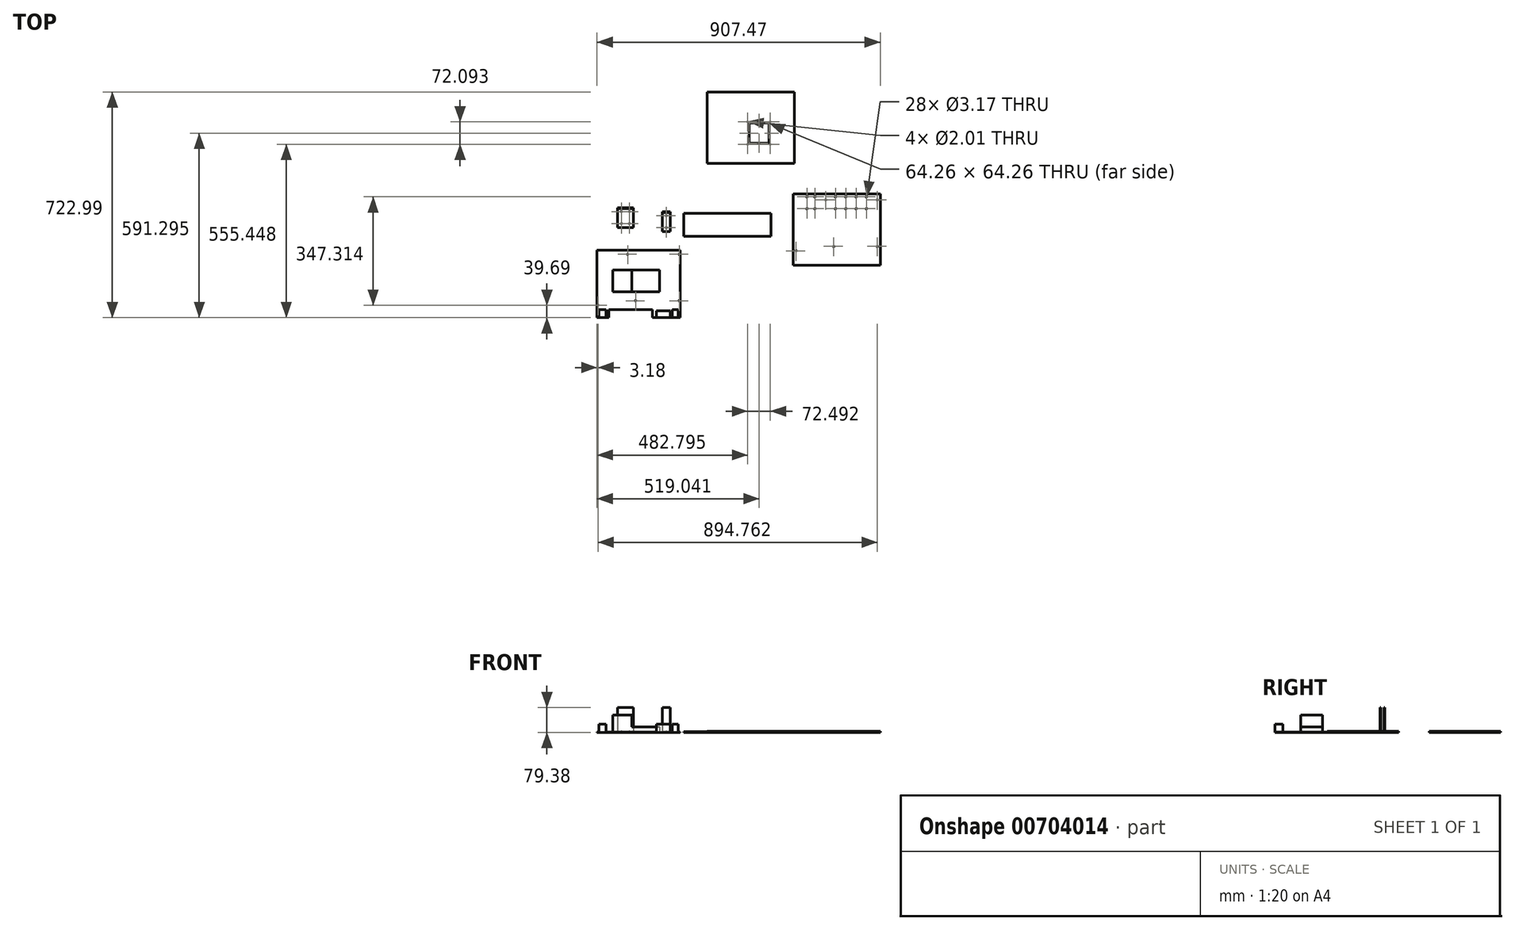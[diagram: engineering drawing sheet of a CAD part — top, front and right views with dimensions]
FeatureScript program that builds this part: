
annotation { "Feature Type Name" : "Feature", "Feature Type Description" : "" }
export const myFeature = defineFeature(function(context is Context, id is Id, definition is map)
    precondition{}
    {
        {
            var Q0;
            Q0=qCreatedBy(makeId("Top.planeOp"),FACE);
            var sketch = newSketch(context, id + "F0", { "sketchPlane" : qUnion([Q0])});
            skLineSegment(sketch, "E0.bottom", {"start": v(-132.8, 35.4) * mm, "end": v(133.9, 35.4) * mm});
            skLineSegment(sketch, "E0.left", {"start": v(-132.8, 35.4) * mm, "end": v(-132.8, -180.5) * mm});
            skLineSegment(sketch, "E0.right", {"start": v(133.9, 35.4) * mm, "end": v(133.9, -180.5) * mm});
            skPoint(sketch, "E1", {"position": v(-94.7, -180.5) * mm});
            skPoint(sketch, "E2", {"position": v(-94.7, -155.1) * mm});
            skLineSegment(sketch, "E3", {"start": v(-94.7, -155.1) * mm, "end": v(-94.7, -180.5) * mm});
            skPoint(sketch, "E4", {"position": v(45, -155.1) * mm});
            skPoint(sketch, "E5", {"position": v(45, -180.5) * mm});
            skLineSegment(sketch, "E6", {"start": v(-94.7, -155.1) * mm, "end": v(45, -155.1) * mm});
            skLineSegment(sketch, "E7", {"start": v(-94.7, -180.5) * mm, "end": v(-132.8, -180.5) * mm});
            skLineSegment(sketch, "E8", {"start": v(45, -180.5) * mm, "end": v(133.9, -180.5) * mm});
            skLineSegment(sketch, "E9", {"start": v(45, -155.1) * mm, "end": v(45, -180.5) * mm});
            skSolve(sketch);
        }
        {
            var Q0;
            Q0=makeQuery(id+"F0.imprint","IMPRINT",FACE,{"disambiguationData":[TD([[makeQuery(id+"F0.imprint","IMPRINT",EDGE,{"derivedFrom":sQuery(id+"F0.wireOp",EDGE,"E0.bottom")}),-1.0]])]});
            var Q1;
            Q1 = qSketchRegion(id + "F15", true);
            extrude(context, id + "F1", {"entities" : qUnion([Q0, Q1]), "depth" : 1.59 * mm, "offsetDistance" : 25.4 * mm});
        }
        {
            var Q0;
            Q0=makeQuery(id+"F1.opExtrude","CAP_FACE",FACE,{"disambiguationData":[OSD([sQuery(id+"F0.wireOp",EDGE,"E0.bottom"),sQuery(id+"F0.wireOp",EDGE,"E0.left"),sQuery(id+"F0.wireOp",EDGE,"E0.right"),sQuery(id+"F0.wireOp",EDGE,"E3"),sQuery(id+"F0.wireOp",EDGE,"E6"),sQuery(id+"F0.wireOp",EDGE,"E7"),sQuery(id+"F0.wireOp",EDGE,"E8"),sQuery(id+"F0.wireOp",EDGE,"E9")])],"isStart":false});
            var sketch = newSketch(context, id + "F2", { "sketchPlane" : qUnion([Q0])});
            skPoint(sketch, "E10", {"position": v(-132.8, -180.5) * mm});
            skPoint(sketch, "E11", {"position": v(-126.45, -180.5) * mm});
            skPoint(sketch, "E12", {"position": v(-126.45, -155.1) * mm});
            skPoint(sketch, "E13", {"position": v(-104.22, -155.1) * mm});
            skPoint(sketch, "E14", {"position": v(-104.22, -180.5) * mm});
            skLineSegment(sketch, "E15", {"start": v(-126.45, -155.1) * mm, "end": v(-104.22, -155.1) * mm});
            skLineSegment(sketch, "E16", {"start": v(-104.22, -155.1) * mm, "end": v(-104.22, -180.5) * mm});
            skLineSegment(sketch, "E17", {"start": v(-104.22, -180.5) * mm, "end": v(-126.45, -180.5) * mm});
            skLineSegment(sketch, "E18", {"start": v(-126.45, -180.5) * mm, "end": v(-126.45, -155.1) * mm});
            skLineSegment(sketch, "E19", {"start": v(-132.8, -180.5) * mm, "end": v(-126.45, -180.5) * mm});
            skPoint(sketch, "E20", {"position": v(-94.7, -180.5) * mm});
            skLineSegment(sketch, "E21", {"start": v(-94.7, -180.5) * mm, "end": v(-104.22, -180.5) * mm});
            skPoint(sketch, "E22", {"position": v(57.7, -180.5) * mm});
            skPoint(sketch, "E23", {"position": v(45, -180.5) * mm});
            skPoint(sketch, "E24", {"position": v(102.15, -180.5) * mm});
            skPoint(sketch, "E25", {"position": v(108.5, -180.5) * mm});
            skPoint(sketch, "E26", {"position": v(127.55, -180.5) * mm});
            skPoint(sketch, "E27", {"position": v(133.9, -180.5) * mm});
            skPoint(sketch, "E28", {"position": v(57.7, -158.28) * mm});
            skPoint(sketch, "E29", {"position": v(102.15, -158.28) * mm});
            skPoint(sketch, "E30", {"position": v(108.4, -155.1) * mm});
            skPoint(sketch, "E31", {"position": v(127.55, -155.1) * mm});
            skLineSegment(sketch, "E32", {"start": v(57.7, -180.5) * mm, "end": v(57.7, -158.28) * mm});
            skLineSegment(sketch, "E33", {"start": v(102.15, -158.28) * mm, "end": v(57.7, -158.28) * mm});
            skLineSegment(sketch, "E34", {"start": v(102.15, -180.5) * mm, "end": v(102.15, -158.28) * mm});
            skLineSegment(sketch, "E35", {"start": v(108.4, -155.1) * mm, "end": v(108.5, -180.5) * mm});
            skLineSegment(sketch, "E36", {"start": v(108.4, -155.1) * mm, "end": v(127.55, -155.1) * mm});
            skLineSegment(sketch, "E37", {"start": v(127.55, -180.5) * mm, "end": v(127.55, -155.1) * mm});
            skLineSegment(sketch, "E38", {"start": v(108.5, -180.5) * mm, "end": v(127.55, -180.5) * mm});
            skLineSegment(sketch, "E39", {"start": v(102.15, -180.5) * mm, "end": v(57.7, -180.5) * mm});
            skSolve(sketch);
        }
        {
            var Q0;
            Q0=makeQuery(id+"F2.imprint","IMPRINT",FACE,{"disambiguationData":[TD([[makeQuery(id+"F2.imprint","IMPRINT",EDGE,{"derivedFrom":sQuery(id+"F2.wireOp",EDGE,"E15")}),-1.0]])]});
            extrude(context, id + "F3", {"entities" : qUnion([Q0]), "operationType" : NewBodyOperationType.ADD, "depth" : 22.22 * mm, "offsetDistance" : 25.4 * mm});
        }
        {
            var Q0;
            Q0 = qSketchRegion(id + "F2", true);
            extrude(context, id + "F4", {"entities" : qUnion([Q0]), "operationType" : NewBodyOperationType.ADD, "depth" : 25.4 * mm, "offsetDistance" : 25.4 * mm});
        }
        {
            var Q0;
            Q0=makeQuery(id+"F1.opExtrude","CAP_FACE",FACE,{"disambiguationData":[OSD([sQuery(id+"F0.wireOp",EDGE,"E0.bottom"),sQuery(id+"F0.wireOp",EDGE,"E0.left"),sQuery(id+"F0.wireOp",EDGE,"E0.right"),sQuery(id+"F0.wireOp",EDGE,"E3"),sQuery(id+"F0.wireOp",EDGE,"E6"),sQuery(id+"F0.wireOp",EDGE,"E7"),sQuery(id+"F0.wireOp",EDGE,"E8"),sQuery(id+"F0.wireOp",EDGE,"E9")])],"isStart":false});
            var sketch = newSketch(context, id + "F5", { "sketchPlane" : qUnion([Q0])});
            skPoint(sketch, "E40", {"position": v(-82, -97.96) * mm});
            skPoint(sketch, "E41", {"position": v(-82, -28.1) * mm});
            skPoint(sketch, "E42", {"position": v(-21.67, -28.1) * mm});
            skPoint(sketch, "E43", {"position": v(-21.67, -97.96) * mm});
            skLineSegment(sketch, "E44", {"start": v(-82, -97.96) * mm, "end": v(-21.67, -97.96) * mm});
            skLineSegment(sketch, "E45", {"start": v(-21.67, -28.1) * mm, "end": v(-21.67, -97.96) * mm});
            skLineSegment(sketch, "E46", {"start": v(-21.67, -28.1) * mm, "end": v(-82, -28.1) * mm});
            skLineSegment(sketch, "E47", {"start": v(-82, -97.96) * mm, "end": v(-82, -28.1) * mm});
            skPoint(sketch, "E48", {"position": v(67.23, -97.96) * mm});
            skPoint(sketch, "E49", {"position": v(67.23, -28.1) * mm});
            skLineSegment(sketch, "E50", {"start": v(-21.67, -97.96) * mm, "end": v(67.23, -97.96) * mm});
            skLineSegment(sketch, "E51", {"start": v(67.23, -28.1) * mm, "end": v(67.23, -97.96) * mm});
            skLineSegment(sketch, "E52", {"start": v(67.23, -28.1) * mm, "end": v(-21.67, -28.1) * mm});
            skSolve(sketch);
        }
        {
            var Q0;
            Q0=makeQuery(id+"F5.imprint","IMPRINT",FACE,{"disambiguationData":[TD([[makeQuery(id+"F5.imprint","IMPRINT",EDGE,{"derivedFrom":sQuery(id+"F5.wireOp",EDGE,"E45")}),1.0]])]});
            extrude(context, id + "F6", {"entities" : qUnion([Q0]), "operationType" : NewBodyOperationType.ADD, "depth" : 15.88 * mm, "offsetDistance" : 25.4 * mm});
        }
        {
            var Q0;
            Q0=makeQuery(id+"F1.opExtrude","CAP_FACE",FACE,{"disambiguationData":[OSD([sQuery(id+"F0.wireOp",EDGE,"E0.bottom"),sQuery(id+"F0.wireOp",EDGE,"E0.left"),sQuery(id+"F0.wireOp",EDGE,"E0.right"),sQuery(id+"F0.wireOp",EDGE,"E3"),sQuery(id+"F0.wireOp",EDGE,"E6"),sQuery(id+"F0.wireOp",EDGE,"E7"),sQuery(id+"F0.wireOp",EDGE,"E8"),sQuery(id+"F0.wireOp",EDGE,"E9")])],"isStart":false});
            var sketch = newSketch(context, id + "F7", { "sketchPlane" : qUnion([Q0])});
            skPoint(sketch, "E53", {"position": v(-82, -97.96) * mm});
            skPoint(sketch, "E54", {"position": v(-82, -28.1) * mm});
            skLineSegment(sketch, "E55", {"start": v(-82, -97.96) * mm, "end": v(-21.67, -97.96) * mm});
            skLineSegment(sketch, "E56", {"start": v(-21.67, -28.1) * mm, "end": v(-82, -28.1) * mm});
            skLineSegment(sketch, "E57", {"start": v(-82, -97.96) * mm, "end": v(-82, -28.1) * mm});
            skLineSegment(sketch, "E58", {"start": v(-21.67, -97.96) * mm, "end": v(-21.67, -28.1) * mm});
            skSolve(sketch);
        }
        {
            var Q0;
            Q0 = qSketchRegion(id + "F7", true);
            extrude(context, id + "F8", {"entities" : qUnion([Q0]), "operationType" : NewBodyOperationType.ADD, "depth" : 53.97 * mm, "offsetDistance" : 25.4 * mm});
        }
        {
            var Q0;
            Q0=qCreatedBy(makeId("Top.planeOp"),FACE);
            var sketch = newSketch(context, id + "F9", { "sketchPlane" : qUnion([Q0])});
            skLineSegment(sketch, "E59.bottom", {"start": v(495.27, 216.02) * mm, "end": v(774.67, 216.02) * mm});
            skLineSegment(sketch, "E59.left", {"start": v(495.27, 216.02) * mm, "end": v(495.27, -12.58) * mm});
            skLineSegment(sketch, "E59.right", {"start": v(774.67, 216.02) * mm, "end": v(774.67, -12.58) * mm});
            skPoint(sketch, "E60", {"position": v(539.72, -12.58) * mm});
            skPoint(sketch, "E61", {"position": v(692.12, -12.58) * mm});
            skLineSegment(sketch, "E62", {"start": v(539.72, -12.58) * mm, "end": v(495.27, -12.58) * mm});
            skLineSegment(sketch, "E63", {"start": v(692.12, -12.58) * mm, "end": v(774.67, -12.58) * mm});
            skLineSegment(sketch, "E64", {"start": v(539.72, -12.58) * mm, "end": v(692.12, -12.58) * mm});
            skLineSegment(sketch, "E65", {"start": v(539.72, 19.17) * mm, "end": v(692.12, 19.17) * mm});
            skSolve(sketch);
        }
        {
            var Q0;
            Q0=makeQuery(id+"F9.imprint","IMPRINT",FACE,{"disambiguationData":[TD([[makeQuery(id+"F9.imprint","IMPRINT",EDGE,{"derivedFrom":sQuery(id+"F9.wireOp",EDGE,"E59.bottom")}),-1.0]])]});
            extrude(context, id + "F10", {"entities" : qUnion([Q0]), "depth" : 3.17 * mm, "offsetDistance" : 25.4 * mm});
        }
        {
            var Q0;
            Q0=qCreatedBy(makeId("Top.planeOp"),FACE);
            var sketch = newSketch(context, id + "F11", { "sketchPlane" : qUnion([Q0])});
            skLineSegment(sketch, "E66.bottom", {"start": v(-67.07, 171.71) * mm, "end": v(-16.27, 171.71) * mm});
            skLineSegment(sketch, "E66.top", {"start": v(-67.07, 108.21) * mm, "end": v(-16.27, 108.21) * mm});
            skLineSegment(sketch, "E66.left", {"start": v(-67.07, 171.71) * mm, "end": v(-67.07, 108.21) * mm});
            skLineSegment(sketch, "E66.right", {"start": v(-16.27, 171.71) * mm, "end": v(-16.27, 108.21) * mm});
            skPoint(sketch, "E67", {"position": v(-16.27, 168.54) * mm});
            skLineSegment(sketch, "E68.bottom", {"start": v(76.73, 158.84) * mm, "end": v(102.13, 158.84) * mm});
            skLineSegment(sketch, "E68.top", {"start": v(76.73, 95.34) * mm, "end": v(102.13, 95.34) * mm});
            skLineSegment(sketch, "E68.left", {"start": v(76.73, 158.84) * mm, "end": v(76.73, 95.34) * mm});
            skLineSegment(sketch, "E68.right", {"start": v(102.13, 158.84) * mm, "end": v(102.13, 95.34) * mm});
            skSolve(sketch);
        }
        {
            var Q0;
            Q0=makeQuery(id+"F11.imprint","IMPRINT",FACE,{"disambiguationData":[TD([[makeQuery(id+"F11.imprint","IMPRINT",EDGE,{"derivedFrom":sQuery(id+"F11.wireOp",EDGE,"E66.bottom")}),-1.0]])]});
            var Q1;
            Q1=makeQuery(id+"F11.imprint","IMPRINT",FACE,{"disambiguationData":[TD([[makeQuery(id+"F11.imprint","IMPRINT",EDGE,{"derivedFrom":sQuery(id+"F11.wireOp",EDGE,"E68.bottom")}),-1.0]])]});
            extrude(context, id + "F12", {"entities" : qUnion([Q0, Q1]), "depth" : 3.17 * mm, "offsetDistance" : 25.4 * mm});
        }
        {
            var Q0;
            Q0=makeQuery(id+"F12.opExtrude","CAP_FACE",FACE,{"disambiguationData":[OSD([sQuery(id+"F11.wireOp",EDGE,"E66.bottom"),sQuery(id+"F11.wireOp",EDGE,"E66.top"),sQuery(id+"F11.wireOp",EDGE,"E66.left"),sQuery(id+"F11.wireOp",EDGE,"E66.right")])],"isStart":false});
            var sketch = newSketch(context, id + "F13", { "sketchPlane" : qUnion([Q0])});
            skPoint(sketch, "E69", {"position": v(-67.07, 168.54) * mm});
            skLineSegment(sketch, "E70", {"start": v(-67.07, 168.54) * mm, "end": v(-16.27, 168.54) * mm});
            skLineSegment(sketch, "E71", {"start": v(-16.27, 168.54) * mm, "end": v(-16.27, 171.71) * mm});
            skLineSegment(sketch, "E72", {"start": v(-16.27, 171.71) * mm, "end": v(-67.07, 171.71) * mm});
            skPoint(sketch, "E73", {"position": v(76.92, 155.68) * mm});
            skPoint(sketch, "E74", {"position": v(76.92, 158.92) * mm});
            skPoint(sketch, "E75", {"position": v(102.18, 158.92) * mm});
            skPoint(sketch, "E76", {"position": v(102.18, 155.68) * mm});
            skLineSegment(sketch, "E77", {"start": v(76.92, 155.68) * mm, "end": v(102.18, 155.68) * mm});
            skLineSegment(sketch, "E78", {"start": v(76.92, 155.68) * mm, "end": v(76.92, 158.92) * mm});
            skLineSegment(sketch, "E79", {"start": v(102.18, 158.92) * mm, "end": v(102.18, 155.68) * mm});
            skLineSegment(sketch, "E80", {"start": v(76.92, 158.92) * mm, "end": v(102.18, 158.92) * mm});
            skSolve(sketch);
        }
        {
            var Q0;
            {var subQ0=sQuery(id+"F13.wireOp",EDGE,"E70");Q0=makeQuery(id+"F13.imprint","IMPRINT",FACE,{"disambiguationData":[TD([[makeQuery(id+"F13.imprint","IMPRINT",EDGE,{"derivedFrom":subQ0}),1.0]])]});}
            extrude(context, id + "F14", {"entities" : qUnion([Q0]), "operationType" : NewBodyOperationType.ADD, "depth" : 76.2 * mm, "offsetDistance" : 25.4 * mm});
        }
        {
            var Q0;
            Q0=makeQuery(id+"F1.opExtrude","CAP_FACE",FACE,{"disambiguationData":[OSD([sQuery(id+"F0.wireOp",EDGE,"E0.bottom"),sQuery(id+"F0.wireOp",EDGE,"E0.left"),sQuery(id+"F0.wireOp",EDGE,"E0.right"),sQuery(id+"F0.wireOp",EDGE,"E3"),sQuery(id+"F0.wireOp",EDGE,"E6"),sQuery(id+"F0.wireOp",EDGE,"E7"),sQuery(id+"F0.wireOp",EDGE,"E8"),sQuery(id+"F0.wireOp",EDGE,"E9")])],"isStart":false});
            var sketch = newSketch(context, id + "F15", { "sketchPlane" : qUnion([Q0])});
            skPoint(sketch, "E81", {"position": v(-129.62, -140.82) * mm});
            skPoint(sketch, "E81.positionSnap0", {"position": v(-129.62, -180.5) * mm});
            skPoint(sketch, "E82", {"position": v(-8.97, -126.53) * mm});
            skPoint(sketch, "E83", {"position": v(130.73, -126.53) * mm});
            skPoint(sketch, "E84", {"position": v(130.73, 22.7) * mm});
            skPoint(sketch, "E85", {"position": v(-34.37, 22.7) * mm});
            skSolve(sketch);
        }
        {
            var Q0;
            Q0=sQuery(id+"F15.wireOp",VERTEX,"E81");
            var Q1;
            Q1=sQuery(id+"F15.wireOp",VERTEX,"E82");
            var Q2;
            Q2=sQuery(id+"F15.wireOp",VERTEX,"E83");
            var Q3;
            Q3=sQuery(id+"F15.wireOp",VERTEX,"E84");
            var Q4;
            Q4=sQuery(id+"F15.wireOp",VERTEX,"E85");
            var Q5;
            Q5=sQuery(id+"F15.wireOp",VERTEX,"a2374fe5-bc82-4061-a760-1ef8f26bc081");
            var Q6;
            Q6=sQuery(id+"F15.wireOp",VERTEX,"47eded31-7bdc-40b9-a985-cf877ede94eb");
            var Q7;
            Q7=sQuery(id+"F15.wireOp",VERTEX,"cbf4bc41-fd4d-44f8-9674-bae50e0a29e2");
            var Q8;
            Q8=sQuery(id+"F15.wireOp",VERTEX,"c512ea41-6fd1-4221-9079-7b53aadaed47");
            var Q9;
            Q9=sQuery(id+"F15.wireOp",VERTEX,"e6fb33bc-7c57-4ffb-9ba9-00cc94939aeb");
            var Q10;
            Q10=makeQuery(id+"F1.opExtrude","SWEPT_BODY",BODY,{"disambiguationData":[OSD([sQuery(id+"F0.wireOp",EDGE,"E0.bottom"),sQuery(id+"F0.wireOp",EDGE,"E0.left"),sQuery(id+"F0.wireOp",EDGE,"E0.right"),sQuery(id+"F0.wireOp",EDGE,"E3"),sQuery(id+"F0.wireOp",EDGE,"E6"),sQuery(id+"F0.wireOp",EDGE,"E7"),sQuery(id+"F0.wireOp",EDGE,"E8"),sQuery(id+"F0.wireOp",EDGE,"E9")])]});
            hole(context, id + "F16", {"style" : HoleStyle.SIMPLE, "endStyle" : HoleEndStyle.THROUGH, "holeDiameter" : 3.17 * mm, "majorDiameter" : 6.35 * mm, "isTappedThrough" : true, "tappedDepth" : 12.7 * mm, "tapClearance" : 3, "locations" : qUnion([Q0, Q1, Q2, Q3, Q4, Q5, Q6, Q7, Q8, Q9]), "scope" : qUnion([Q10])});
        }
        {
            var Q0;
            Q0=makeQuery(id+"F10.opExtrude","CAP_FACE",FACE,{"disambiguationData":[OSD([sQuery(id+"F9.wireOp",EDGE,"E59.bottom"),sQuery(id+"F9.wireOp",EDGE,"E59.left"),sQuery(id+"F9.wireOp",EDGE,"E59.right"),sQuery(id+"F9.wireOp",EDGE,"E62"),sQuery(id+"F9.wireOp",EDGE,"E63"),sQuery(id+"F9.wireOp",EDGE,"E64")])],"isStart":false});
            var sketch = newSketch(context, id + "F17", { "sketchPlane" : qUnion([Q0])});
            skPoint(sketch, "E86", {"position": v(504.8, 33.44) * mm});
            skPoint(sketch, "E87", {"position": v(625.44, 47.74) * mm});
            skPoint(sketch, "E88", {"position": v(765.14, 47.74) * mm});
            skPoint(sketch, "E89", {"position": v(765.14, 196.97) * mm});
            skPoint(sketch, "E90", {"position": v(600.04, 196.97) * mm});
            skPoint(sketch, "E91", {"position": v(539.72, 206.5) * mm});
            skPoint(sketch, "E92", {"position": v(565.12, 206.5) * mm});
            skPoint(sketch, "E93", {"position": v(539.72, 168.4) * mm});
            skPoint(sketch, "E94", {"position": v(565.12, 168.4) * mm});
            skPoint(sketch, "E95", {"position": v(730.22, 206.5) * mm});
            skPoint(sketch, "E96", {"position": v(697.2, 206.5) * mm});
            skPoint(sketch, "E97", {"position": v(664.18, 206.5) * mm});
            skPoint(sketch, "E98", {"position": v(631.16, 206.5) * mm});
            skPoint(sketch, "E99", {"position": v(631.16, 168.4) * mm});
            skPoint(sketch, "E100", {"position": v(664.18, 168.4) * mm});
            skPoint(sketch, "E101", {"position": v(697.2, 168.4) * mm});
            skPoint(sketch, "E102", {"position": v(730.22, 168.4) * mm});
            skSolve(sketch);
        }
        {
            var Q0;
            Q0=sQuery(id+"F17.wireOp",VERTEX,"E86");
            var Q1;
            Q1=sQuery(id+"F17.wireOp",VERTEX,"E87");
            var Q2;
            Q2=sQuery(id+"F17.wireOp",VERTEX,"E88");
            var Q3;
            Q3=sQuery(id+"F17.wireOp",VERTEX,"E89");
            var Q4;
            Q4=sQuery(id+"F17.wireOp",VERTEX,"E90");
            var Q5;
            Q5=sQuery(id+"F17.wireOp",VERTEX,"E94");
            var Q6;
            Q6=sQuery(id+"F17.wireOp",VERTEX,"E92");
            var Q7;
            Q7=sQuery(id+"F17.wireOp",VERTEX,"E91");
            var Q8;
            Q8=sQuery(id+"F17.wireOp",VERTEX,"E93");
            var Q9;
            Q9=sQuery(id+"F17.wireOp",VERTEX,"E98");
            var Q10;
            Q10=sQuery(id+"F17.wireOp",VERTEX,"E97");
            var Q11;
            Q11=sQuery(id+"F17.wireOp",VERTEX,"E96");
            var Q12;
            Q12=sQuery(id+"F17.wireOp",VERTEX,"E95");
            var Q13;
            Q13=sQuery(id+"F17.wireOp",VERTEX,"E100");
            var Q14;
            Q14=sQuery(id+"F17.wireOp",VERTEX,"E101");
            var Q15;
            Q15=sQuery(id+"F17.wireOp",VERTEX,"E102");
            var Q16;
            Q16=sQuery(id+"F17.wireOp",VERTEX,"E99");
            var Q17;
            Q17=makeQuery(id+"F10.opExtrude","SWEPT_BODY",BODY,{"disambiguationData":[OSD([sQuery(id+"F9.wireOp",EDGE,"E59.bottom"),sQuery(id+"F9.wireOp",EDGE,"E59.left"),sQuery(id+"F9.wireOp",EDGE,"E59.right"),sQuery(id+"F9.wireOp",EDGE,"E62"),sQuery(id+"F9.wireOp",EDGE,"E63"),sQuery(id+"F9.wireOp",EDGE,"E64")])]});
            hole(context, id + "F18", {"style" : HoleStyle.SIMPLE, "endStyle" : HoleEndStyle.THROUGH, "holeDiameter" : 3.17 * mm, "majorDiameter" : 6.35 * mm, "isTappedThrough" : true, "tappedDepth" : 12.7 * mm, "tapClearance" : 3, "locations" : qUnion([Q0, Q1, Q2, Q3, Q4, Q5, Q6, Q7, Q8, Q9, Q10, Q11, Q12, Q13, Q14, Q15, Q16]), "scope" : qUnion([Q17])});
        }
        {
            var Q0;
            Q0=makeQuery(id+"F12.opExtrude","CAP_FACE",FACE,{"disambiguationData":[OSD([sQuery(id+"F11.wireOp",EDGE,"E66.bottom"),sQuery(id+"F11.wireOp",EDGE,"E66.top"),sQuery(id+"F11.wireOp",EDGE,"E66.left"),sQuery(id+"F11.wireOp",EDGE,"E66.right")])],"isStart":false});
            var sketch = newSketch(context, id + "F19", { "sketchPlane" : qUnion([Q0])});
            skPoint(sketch, "E103", {"position": v(-54.37, 120.91) * mm});
            skPoint(sketch, "E104", {"position": v(-28.97, 120.91) * mm});
            skPoint(sketch, "E105", {"position": v(-28.83, 159.01) * mm});
            skPoint(sketch, "E106", {"position": v(-54.4, 159.01) * mm});
            skSolve(sketch);
        }
        {
            var Q0;
            Q0=sQuery(id+"F19.wireOp",VERTEX,"E103");
            var Q1;
            Q1=sQuery(id+"F19.wireOp",VERTEX,"E104");
            var Q2;
            Q2=sQuery(id+"F19.wireOp",VERTEX,"E105");
            var Q3;
            Q3=sQuery(id+"F19.wireOp",VERTEX,"E106");
            var Q4;
            Q4=makeQuery(id+"F12.opExtrude","SWEPT_BODY",BODY,{"disambiguationData":[OSD([sQuery(id+"F11.wireOp",EDGE,"E66.bottom"),sQuery(id+"F11.wireOp",EDGE,"E66.top"),sQuery(id+"F11.wireOp",EDGE,"E66.left"),sQuery(id+"F11.wireOp",EDGE,"E66.right")])]});
            hole(context, id + "F20", {"style" : HoleStyle.SIMPLE, "endStyle" : HoleEndStyle.THROUGH, "holeDiameter" : 3.17 * mm, "majorDiameter" : 6.35 * mm, "isTappedThrough" : true, "tappedDepth" : 12.7 * mm, "tapClearance" : 3, "locations" : qUnion([Q0, Q1, Q2, Q3]), "scope" : qUnion([Q4])});
        }
        {
            var Q0;
            Q0=makeQuery(id+"F12.opExtrude","CAP_FACE",FACE,{"disambiguationData":[OSD([sQuery(id+"F11.wireOp",EDGE,"E68.bottom"),sQuery(id+"F11.wireOp",EDGE,"E68.top"),sQuery(id+"F11.wireOp",EDGE,"E68.left"),sQuery(id+"F11.wireOp",EDGE,"E68.right")])],"isStart":false});
            var sketch = newSketch(context, id + "F21", { "sketchPlane" : qUnion([Q0])});
            skPoint(sketch, "E107", {"position": v(76.73, 158.84) * mm});
            skPoint(sketch, "E108", {"position": v(76.73, 155.67) * mm});
            skLineSegment(sketch, "E109", {"start": v(76.73, 158.84) * mm, "end": v(76.73, 155.67) * mm});
            skLineSegment(sketch, "E110", {"start": v(76.73, 155.67) * mm, "end": v(102.13, 155.67) * mm});
            skLineSegment(sketch, "E111", {"start": v(76.73, 158.84) * mm, "end": v(102.13, 158.84) * mm});
            skLineSegment(sketch, "E112", {"start": v(102.13, 158.84) * mm, "end": v(102.13, 155.67) * mm});
            skSolve(sketch);
        }
        {
            var Q0;
            Q0=makeQuery(id+"F21.imprint","IMPRINT",FACE,{"disambiguationData":[TD([[makeQuery(id+"F21.imprint","IMPRINT",EDGE,{"derivedFrom":sQuery(id+"F21.wireOp",EDGE,"E109")}),1.0]])]});
            extrude(context, id + "F22", {"entities" : qUnion([Q0]), "operationType" : NewBodyOperationType.ADD, "depth" : 76.2 * mm, "offsetDistance" : 25.4 * mm});
        }
        {
            var Q0;
            Q0=makeQuery(id+"F12.opExtrude","CAP_FACE",FACE,{"disambiguationData":[OSD([sQuery(id+"F11.wireOp",EDGE,"E68.bottom"),sQuery(id+"F11.wireOp",EDGE,"E68.top"),sQuery(id+"F11.wireOp",EDGE,"E68.left"),sQuery(id+"F11.wireOp",EDGE,"E68.right")])],"isStart":false});
            var sketch = newSketch(context, id + "F23", { "sketchPlane" : qUnion([Q0])});
            skPoint(sketch, "E113", {"position": v(89.43, 108.04) * mm});
            skPoint(sketch, "E114", {"position": v(89.43, 146.14) * mm});
            skSolve(sketch);
        }
        {
            var Q0;
            Q0=sQuery(id+"F23.wireOp",VERTEX,"E114");
            var Q1;
            Q1=sQuery(id+"F23.wireOp",VERTEX,"E113");
            var Q2;
            Q2=makeQuery(id+"F12.opExtrude","SWEPT_BODY",BODY,{"disambiguationData":[OSD([sQuery(id+"F11.wireOp",EDGE,"E68.bottom"),sQuery(id+"F11.wireOp",EDGE,"E68.top"),sQuery(id+"F11.wireOp",EDGE,"E68.left"),sQuery(id+"F11.wireOp",EDGE,"E68.right")])]});
            hole(context, id + "F24", {"style" : HoleStyle.SIMPLE, "endStyle" : HoleEndStyle.THROUGH, "holeDiameter" : 3.17 * mm, "majorDiameter" : 6.35 * mm, "isTappedThrough" : true, "tappedDepth" : 12.7 * mm, "tapClearance" : 3, "locations" : qUnion([Q0, Q1]), "scope" : qUnion([Q2])});
        }
        {
            var Q0;
            Q0=qCreatedBy(makeId("Top.planeOp"),FACE);
            var sketch = newSketch(context, id + "F25", { "sketchPlane" : qUnion([Q0])});
            skLineSegment(sketch, "E115.bottom", {"start": v(145.1, 153.47) * mm, "end": v(424.5, 153.47) * mm});
            skLineSegment(sketch, "E115.top", {"start": v(145.1, 80.45) * mm, "end": v(424.5, 80.45) * mm});
            skLineSegment(sketch, "E115.left", {"start": v(145.1, 153.47) * mm, "end": v(145.1, 80.45) * mm});
            skLineSegment(sketch, "E115.right", {"start": v(424.5, 153.47) * mm, "end": v(424.5, 80.45) * mm});
            skSolve(sketch);
        }
        {
            var Q0;
            Q0=makeQuery(id+"F25.imprint","IMPRINT",FACE,{"disambiguationData":[TD([[makeQuery(id+"F25.imprint","IMPRINT",EDGE,{"derivedFrom":sQuery(id+"F25.wireOp",EDGE,"E115.bottom")}),-1.0]])]});
            extrude(context, id + "F26", {"entities" : qUnion([Q0]), "depth" : 3 * mm, "offsetDistance" : 25.4 * mm});
        }
        {
            var Q0;
            Q0=qCreatedBy(makeId("Top.planeOp"),FACE);
            var sketch = newSketch(context, id + "F27", { "sketchPlane" : qUnion([Q0])});
            skLineSegment(sketch, "E116.bottom", {"start": v(219.5, 542.48) * mm, "end": v(498.9, 542.48) * mm});
            skLineSegment(sketch, "E116.top", {"start": v(219.5, 313.88) * mm, "end": v(498.9, 313.88) * mm});
            skLineSegment(sketch, "E116.left", {"start": v(219.5, 542.48) * mm, "end": v(219.5, 313.88) * mm});
            skLineSegment(sketch, "E116.right", {"start": v(498.9, 542.48) * mm, "end": v(498.9, 313.88) * mm});
            skPoint(sketch, "E117", {"position": v(346.5, 371.03) * mm});
            skPoint(sketch, "E118", {"position": v(426, 371.03) * mm});
            skPoint(sketch, "E119", {"position": v(426, 450.54) * mm});
            skPoint(sketch, "E120", {"position": v(346.5, 450.54) * mm});
            skLineSegment(sketch, "E121", {"start": v(346.5, 371.03) * mm, "end": v(346.5, 450.54) * mm});
            skLineSegment(sketch, "E122", {"start": v(426, 450.54) * mm, "end": v(346.5, 450.54) * mm});
            skLineSegment(sketch, "E123", {"start": v(426, 371.03) * mm, "end": v(426, 450.54) * mm});
            skLineSegment(sketch, "E124", {"start": v(426, 371.03) * mm, "end": v(346.5, 371.03) * mm});
            skPoint(sketch, "E125", {"position": v(354.11, 442.92) * mm});
            skPoint(sketch, "E126", {"position": v(418.37, 442.92) * mm});
            skPoint(sketch, "E127", {"position": v(418.37, 378.65) * mm});
            skPoint(sketch, "E128", {"position": v(354.11, 378.65) * mm});
            skLineSegment(sketch, "E129", {"start": v(354.11, 442.92) * mm, "end": v(418.37, 442.92) * mm});
            skLineSegment(sketch, "E130", {"start": v(418.37, 442.92) * mm, "end": v(418.37, 378.65) * mm});
            skLineSegment(sketch, "E131", {"start": v(418.37, 378.65) * mm, "end": v(354.11, 378.65) * mm});
            skLineSegment(sketch, "E132", {"start": v(354.11, 378.65) * mm, "end": v(354.11, 442.92) * mm});
            skPoint(sketch, "E133", {"position": v(350, 447.03) * mm});
            skPoint(sketch, "E134", {"position": v(422.49, 447.03) * mm});
            skPoint(sketch, "E135", {"position": v(422.49, 374.54) * mm});
            skPoint(sketch, "E136", {"position": v(350, 374.54) * mm});
            skSolve(sketch);
        }
        {
            var Q0;
            Q0=makeQuery(id+"F27.imprint","IMPRINT",FACE,{"disambiguationData":[TD([[makeQuery(id+"F27.imprint","IMPRINT",EDGE,{"derivedFrom":sQuery(id+"F27.wireOp",EDGE,"E116.bottom")}),-1.0]])]});
            var Q1;
            Q1=makeQuery(id+"F27.imprint","IMPRINT",FACE,{"disambiguationData":[TD([[makeQuery(id+"F27.imprint","IMPRINT",EDGE,{"derivedFrom":sQuery(id+"F27.wireOp",EDGE,"E121")}),-1.0]])]});
            extrude(context, id + "F28", {"entities" : qUnion([Q0, Q1]), "depth" : 3.17 * mm, "offsetDistance" : 25.4 * mm});
        }
        {
            var Q0;
            Q0=makeQuery(id+"F28.opExtrude","CAP_FACE",FACE,{"disambiguationData":[OSD([sQuery(id+"F27.wireOp",EDGE,"E116.bottom"),sQuery(id+"F27.wireOp",EDGE,"E116.top"),sQuery(id+"F27.wireOp",EDGE,"E116.left"),sQuery(id+"F27.wireOp",EDGE,"E116.right"),sQuery(id+"F27.wireOp",EDGE,"E129"),sQuery(id+"F27.wireOp",EDGE,"E130"),sQuery(id+"F27.wireOp",EDGE,"E131"),sQuery(id+"F27.wireOp",EDGE,"E132")])],"isStart":false});
            var sketch = newSketch(context, id + "F29", { "sketchPlane" : qUnion([Q0])});
            skPoint(sketch, "E137", {"position": v(-105.54, -22.71) * mm});
            skPoint(sketch, "E138", {"position": v(-6.13, -22.71) * mm});
            skPoint(sketch, "E139", {"position": v(-6.13, -122.13) * mm});
            skPoint(sketch, "E140", {"position": v(-105.54, -122.13) * mm});
            skPoint(sketch, "E141", {"position": v(426, 450.54) * mm});
            skPoint(sketch, "E142", {"position": v(346.5, 450.54) * mm});
            skPoint(sketch, "E143", {"position": v(346.5, 371.03) * mm});
            skPoint(sketch, "E144", {"position": v(354.11, 378.65) * mm});
            skPoint(sketch, "E145", {"position": v(418.37, 378.65) * mm});
            skPoint(sketch, "E146", {"position": v(418.37, 442.92) * mm});
            skPoint(sketch, "E147", {"position": v(426, 371.03) * mm});
            skPoint(sketch, "E148", {"position": v(350, 447.03) * mm});
            skPoint(sketch, "E149", {"position": v(422.49, 447.03) * mm});
            skPoint(sketch, "E150", {"position": v(422.49, 374.94) * mm});
            skPoint(sketch, "E151", {"position": v(350, 374.94) * mm});
            skSolve(sketch);
        }
        {
            var Q0;
            Q0=sQuery(id+"F29.wireOp",VERTEX,"E148");
            var Q1;
            Q1=sQuery(id+"F29.wireOp",VERTEX,"E149");
            var Q2;
            Q2=sQuery(id+"F29.wireOp",VERTEX,"E150");
            var Q3;
            Q3=sQuery(id+"F29.wireOp",VERTEX,"E151");
            var Q4;
            Q4=makeQuery(id+"F28.opExtrude","SWEPT_BODY",BODY,{"disambiguationData":[OSD([sQuery(id+"F27.wireOp",EDGE,"E116.bottom"),sQuery(id+"F27.wireOp",EDGE,"E116.top"),sQuery(id+"F27.wireOp",EDGE,"E116.left"),sQuery(id+"F27.wireOp",EDGE,"E116.right"),sQuery(id+"F27.wireOp",EDGE,"E129"),sQuery(id+"F27.wireOp",EDGE,"E130"),sQuery(id+"F27.wireOp",EDGE,"E131"),sQuery(id+"F27.wireOp",EDGE,"E132")])]});
            hole(context, id + "F30", {"style" : HoleStyle.SIMPLE, "endStyle" : HoleEndStyle.THROUGH, "holeDiameter" : 2 * mm, "majorDiameter" : 6.35 * mm, "isTappedThrough" : true, "tappedDepth" : 12.7 * mm, "tapClearance" : 3, "locations" : qUnion([Q0, Q1, Q2, Q3]), "scope" : qUnion([Q4])});
        }
    });
